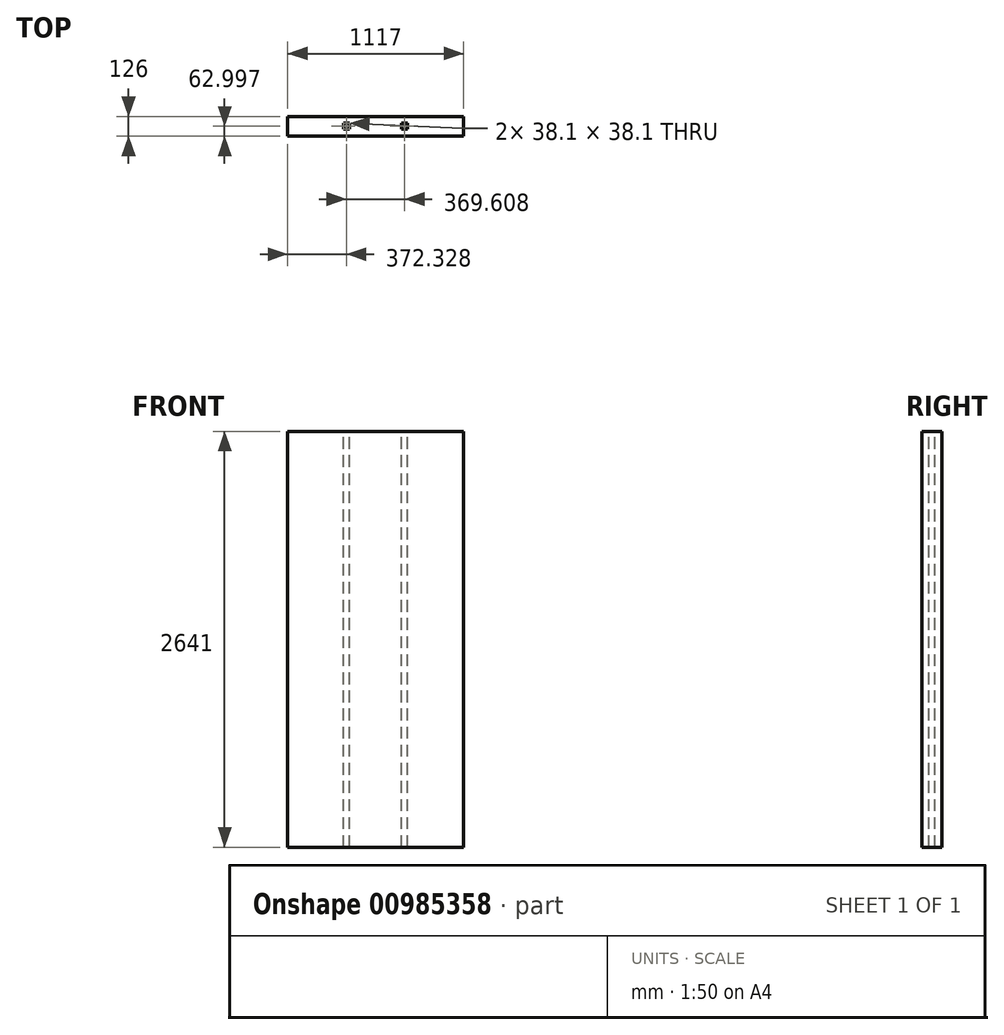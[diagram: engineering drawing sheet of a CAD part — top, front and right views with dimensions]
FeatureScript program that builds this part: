
annotation { "Feature Type Name" : "Feature", "Feature Type Description" : "" }
export const myFeature = defineFeature(function(context is Context, id is Id, definition is map)
    precondition{}
    {
        {
            var Q0;
            Q0=qCreatedBy(makeId("Top.planeOp"),FACE);
            var sketch = newSketch(context, id + "F0", { "sketchPlane" : qUnion([Q0])});
            skLineSegment(sketch, "E0.bottom", {"start": v(-553.02, -89.14) * mm, "end": v(563.98, -89.14) * mm});
            skLineSegment(sketch, "E0.top", {"start": v(-553.02, -215.14) * mm, "end": v(563.98, -215.14) * mm});
            skLineSegment(sketch, "E0.left", {"start": v(-553.02, -89.14) * mm, "end": v(-553.02, -215.14) * mm});
            skLineSegment(sketch, "E0.right", {"start": v(563.98, -89.14) * mm, "end": v(563.98, -215.14) * mm});
            skSolve(sketch);
        }
        {
            var Q0;
            Q0=makeQuery(id+"F0.imprint","IMPRINT",FACE,{"disambiguationData":[TD([[makeQuery(id+"F0.imprint","IMPRINT",EDGE,{"derivedFrom":sQuery(id+"F0.wireOp",EDGE,"E0.bottom")}),-1.0]])]});
            extrude(context, id + "F1", {"entities" : qUnion([Q0]), "depth" : 2641 * mm, "offsetDistance" : 25 * mm});
        }
        {
            var Q0;
            Q0=makeQuery(id+"F1.opExtrude","CAP_FACE",FACE,{"disambiguationData":[OSD([sQuery(id+"F0.wireOp",EDGE,"E0.bottom"),sQuery(id+"F0.wireOp",EDGE,"E0.top"),sQuery(id+"F0.wireOp",EDGE,"E0.left"),sQuery(id+"F0.wireOp",EDGE,"E0.right")])],"isStart":false});
            var sketch = newSketch(context, id + "F2", { "sketchPlane" : qUnion([Q0])});
            skLineSegment(sketch, "E1.bottom", {"start": v(-199.74, -133.1) * mm, "end": v(-161.64, -133.1) * mm});
            skLineSegment(sketch, "E1.top", {"start": v(-199.74, -171.2) * mm, "end": v(-161.64, -171.2) * mm});
            skLineSegment(sketch, "E1.left", {"start": v(-199.74, -133.1) * mm, "end": v(-199.74, -171.2) * mm});
            skLineSegment(sketch, "E1.right", {"start": v(-161.64, -133.1) * mm, "end": v(-161.64, -171.2) * mm});
            skPoint(sketch, "E2.firstSnap0", {"position": v(-161.64, -152.14) * mm});
            skLineSegment(sketch, "E3.bottom", {"start": v(169.87, -133.1) * mm, "end": v(207.97, -133.1) * mm});
            skLineSegment(sketch, "E3.top", {"start": v(169.87, -171.2) * mm, "end": v(207.97, -171.2) * mm});
            skLineSegment(sketch, "E3.left", {"start": v(169.87, -133.1) * mm, "end": v(169.87, -171.2) * mm});
            skLineSegment(sketch, "E3.right", {"start": v(207.97, -133.1) * mm, "end": v(207.97, -171.2) * mm});
            skSolve(sketch);
        }
        {
            var Q0;
            Q0 = qSketchRegion(id + "F2", true);
            extrude(context, id + "F3", {"entities" : qUnion([Q0]), "operationType" : NewBodyOperationType.REMOVE, "endBound" : BoundingType.THROUGH_ALL, "oppositeDirection" : true, "depth" : 25 * mm, "offsetDistance" : 25 * mm});
        }
    });
